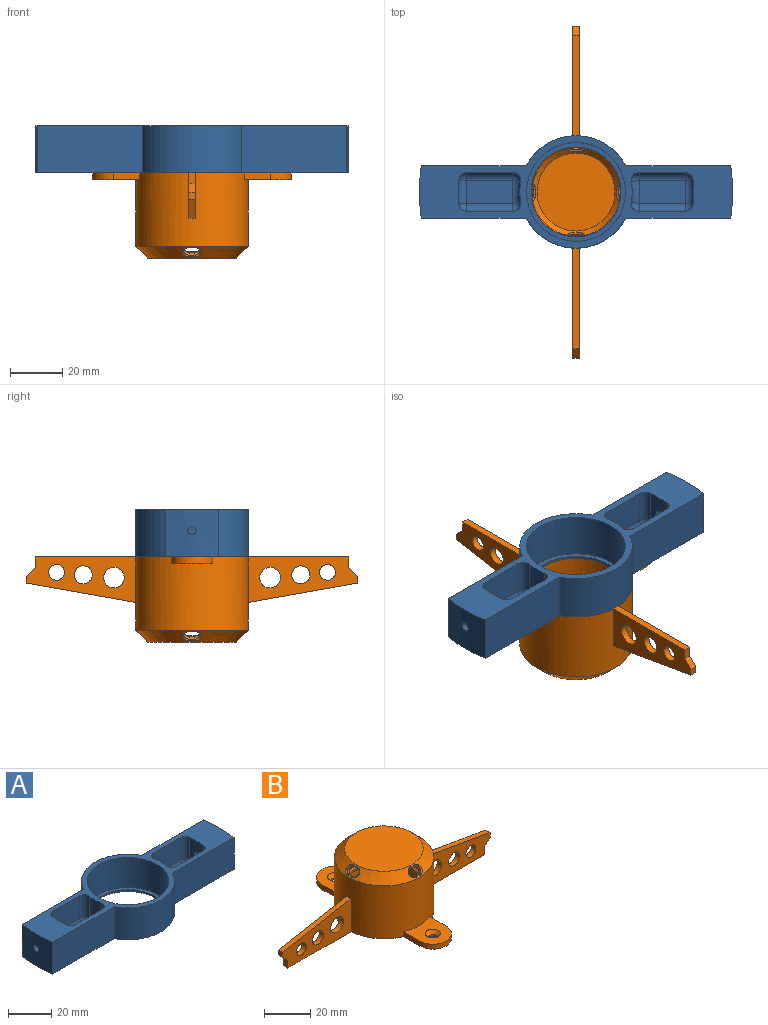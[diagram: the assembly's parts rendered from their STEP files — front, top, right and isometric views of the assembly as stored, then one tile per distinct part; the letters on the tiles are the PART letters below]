
ASSEMBLY  parts=2 mates=1
PART A: 49 faces, bbox 120x43x18 mm
  f0: cylinder r=60mm len=20mm, axis (0,0,-1), area 353.6mm2, adj f5,f10,f11,f12,f48
  f1: cylinder r=45mm len=12.6mm, axis (0,0,1), area 111mm2, adj f11,f36,f42,f43,f48
  f2: cylinder r=60mm len=20mm, axis (0,0,-1), area 353.6mm2, adj f7,f8,f11,f12,f47
  f3: cylinder r=45mm len=12.6mm, axis (0,0,1), area 111mm2, adj f11,f29,f30,f34,f47
  f4: cylinder r=17.2mm len=34.4mm, axis (0,0,-1), area 108.1mm2, adj f12,f21
  f5: plane 40.13x18mm, normal (0,-1,0), area 722.3mm2, adj f0,f6,f11,f12
  f6: cylinder r=21.5mm len=38.07mm, axis (0,0,-1), area 841.4mm2, adj f5,f7,f11,f12
  f7: plane 40.13x18mm, normal (0,-1,0), area 722.3mm2, adj f2,f6,f11,f12
  f8: plane 40.13x18mm, normal (0,1,0), area 722.3mm2, adj f2,f9,f11,f12
  f9: cylinder r=21.5mm len=38.07mm, axis (0,0,-1), area 841.4mm2, adj f8,f10,f11,f12
  f10: plane 40.13x18mm, normal (0,1,0), area 722.3mm2, adj f0,f9,f11,f12
  f11: plane 120x43mm, normal (0,0,1), area 1207.4mm2, adj f0,f1,f2,f3,f5,f6,f7,f8
  f12: plane 120x43mm, normal (0,0,-1), area 2083.7mm2, adj f0,f2,f4,f5,f6,f7,f8,f9
  f13: plane 17.9x8.8mm, normal (0,0,1), area 154.5mm2, adj f25,f28,f31,f34
  f14: plane 17.67x12.6mm, normal (0,1,0), area 222.6mm2, adj f11,f24,f30,f31
  f15: plane 17.67x12.6mm, normal (0,-1,0), area 222.6mm2, adj f11,f23,f28,f29
  f16: cylinder r=21.5mm len=12.6mm, axis (0,0,1), area 97.8mm2, adj f11,f23,f24,f25
  f17: plane 17.9x8.8mm, normal (0,0,1), area 154.5mm2, adj f37,f40,f43,f46
  f18: plane 17.67x12.6mm, normal (0,-1,0), area 222.6mm2, adj f11,f35,f36,f37
  f19: plane 17.67x12.6mm, normal (0,1,0), area 222.6mm2, adj f11,f41,f42,f46
  f20: cylinder r=21.5mm len=12.6mm, axis (0,0,1), area 97.8mm2, adj f11,f35,f40,f41
  f21: plane 37.8x37.8mm, normal (0,0,1), area 192.8mm2, adj f4,f22
  f22: cylinder r=18.9mm len=37.8mm, axis (0,0,1), area 2018.8mm2, adj f11,f21
  f23: cylinder r=3mm len=12.6mm, axis (0,0,1), area 66.2mm2, adj f11,f15,f16,f26
  f24: cylinder r=3mm len=12.6mm, axis (0,0,1), area 66.2mm2, adj f11,f14,f16,f27
  f25: torus R=24.5mm, axis (0,0,1), area 38.4mm2, adj f13,f16,f26,f27
  f26: sphere r=3mm, area 15.8mm2, adj f23,f25,f28
  f27: sphere r=3mm, area 15.8mm2, adj f24,f25,f31
  f28: cylinder r=3mm len=17.67mm, axis (1,0,0), area 83.3mm2, adj f13,f15,f26,f32
  f29: cylinder r=3mm len=12.6mm, axis (0,0,1), area 55.4mm2, adj f3,f11,f15,f32
  f30: cylinder r=3mm len=12.6mm, axis (0,0,1), area 55.4mm2, adj f3,f11,f14,f33
  f31: cylinder r=3mm len=17.67mm, axis (-1,0,0), area 83.3mm2, adj f13,f14,f27,f33
  f32: sphere r=3mm, area 13.2mm2, adj f28,f29,f34
  f33: sphere r=3mm, area 13.2mm2, adj f30,f31,f34
  f34: torus R=42mm, axis (0,0,1), area 43.4mm2, adj f3,f13,f32,f33
  f35: cylinder r=3mm len=12.6mm, axis (0,0,1), area 66.2mm2, adj f11,f18,f20,f38
  f36: cylinder r=3mm len=12.6mm, axis (0,0,1), area 55.4mm2, adj f1,f11,f18,f39
  f37: cylinder r=3mm len=17.67mm, axis (1,0,0), area 83.3mm2, adj f17,f18,f38,f39
  f38: sphere r=3mm, area 15.8mm2, adj f35,f37,f40
  f39: sphere r=3mm, area 13.2mm2, adj f36,f37,f43
  f40: torus R=24.5mm, axis (0,0,1), area 38.4mm2, adj f17,f20,f38,f44
  f41: cylinder r=3mm len=12.6mm, axis (0,0,1), area 66.2mm2, adj f11,f19,f20,f44
  f42: cylinder r=3mm len=12.6mm, axis (0,0,1), area 55.4mm2, adj f1,f11,f19,f45
  f43: torus R=42mm, axis (0,0,1), area 43.4mm2, adj f1,f17,f39,f45
  f44: sphere r=3mm, area 15.8mm2, adj f40,f41,f46
  f45: sphere r=3mm, area 13.2mm2, adj f42,f43,f46
  f46: cylinder r=3mm len=17.67mm, axis (-1,0,0), area 83.3mm2, adj f17,f19,f44,f45
  f47: cylinder r=1.6mm len=15.03mm, axis (-1,0,0), area 150.8mm2, adj f2,f3
  f48: cylinder r=1.6mm len=15.03mm, axis (1,0,0), area 150.8mm2, adj f0,f1
PART B: 89 faces, bbox 127x75.9x32.6 mm
  f0: cylinder r=21.5mm len=43mm, axis (0,0,-1), area 3617mm2, adj f2,f4,f5,f6,f8,f9,f11,f12
  f1: cylinder r=60mm len=4.01mm, axis (0,0,-1), area 10.4mm2, adj f5,f9,f12,f68
  f2: cone r=21.5mm half-angle=45deg, axis (0,0,-1), area 639.7mm2, adj f0,f13,f23,f24,f25,f26,f35,f36
  f3: cone r=18.9mm half-angle=45deg, axis (0,0,-1), area 644.6mm2, adj f17,f18,f27,f28,f29,f30,f39,f40
  f4: plane 42.04x7.42mm, normal (-0.17,0,0.98), area 110.9mm2, adj f0,f5,f9,f67
  f5: plane 42.03x17.41mm, normal (0,-1,0), area 440.6mm2, adj f0,f1,f4,f12,f67,f68,f83,f84
  f6: plane 42.03x17.41mm, normal (0,-1,0), area 440.6mm2, adj f0,f7,f11,f12,f69,f70,f86,f87
  f7: cylinder r=60mm len=4.01mm, axis (0,0,-1), area 10.4mm2, adj f6,f8,f12,f70
  f8: plane 42.03x17.41mm, normal (0,1,0), area 440.6mm2, adj f0,f7,f11,f12,f69,f70,f86,f87
  f9: plane 42.03x17.41mm, normal (0,1,0), area 440.6mm2, adj f0,f1,f4,f12,f67,f68,f83,f84
  f10: cylinder r=18.9mm len=37.8mm, axis (0,0,-1), area 1294.4mm2, adj f12,f14
  f11: plane 42.04x7.42mm, normal (0.17,0,0.98), area 110.9mm2, adj f0,f6,f8,f69
  f12: plane 120x75.91mm, normal (0,0,-1), area 1002mm2, adj f0,f1,f5,f6,f7,f8,f9,f10
  f13: plane 33.95x33.95mm, normal (0,0,1), area 905.5mm2, adj f2
  f14: cone r=18.9mm half-angle=45deg, axis (0,0,-1), area 318.1mm2, adj f10,f15
  f15: cylinder r=16.9mm len=33.8mm, axis (0,0,1), area 106.2mm2, adj f14,f16
  f16: cone r=16.9mm half-angle=45deg, axis (0,0,1), area 490.5mm2, adj f15,f17
  f17: cylinder r=19.9mm len=39.8mm, axis (0,0,1), area 1137.8mm2, adj f3,f16
  f18: plane 29.8x29.8mm, normal (0,0,-1), area 697.5mm2, adj f3
  f19: plane 2.2x1.15mm, normal (0,-0.71,-0.71), area 3.5mm2, adj f20,f22,f26,f30
  f20: cylinder r=2.1mm len=4.28mm, axis (0,0.71,-0.71), area 10.6mm2, adj f19,f21,f24,f28
  f21: plane 2.2x1.15mm, normal (0,0.71,0.71), area 3.5mm2, adj f20,f22,f23,f27
  f22: cylinder r=2.1mm len=4.28mm, axis (0,0.71,-0.71), area 10.6mm2, adj f19,f21,f25,f29
  f23: bspline ~11.26x1.06mm, area 1.7mm2, adj f2,f21,f24,f25
  f24: bspline ~3.69x3.68mm, area 5.9mm2, adj f2,f20,f23,f26
  f25: bspline ~3.69x3.68mm, area 5.9mm2, adj f2,f22,f23,f26
  f26: bspline ~11.33x1.14mm, area 1.8mm2, adj f2,f19,f24,f25
  f27: bspline ~11.08x1.08mm, area 1.7mm2, adj f3,f21,f28,f29
  f28: bspline ~3.69x3.68mm, area 5.3mm2, adj f3,f20,f27,f30
  f29: bspline ~3.69x3.68mm, area 5.3mm2, adj f3,f22,f27,f30
  f30: bspline ~11.12x1.15mm, area 1.7mm2, adj f3,f19,f28,f29
  f31: plane 2.2x1.15mm, normal (0.71,0,-0.71), area 3.5mm2, adj f32,f34,f38,f42
  f32: cylinder r=2.1mm len=4.28mm, axis (-0.71,0,-0.71), area 10.6mm2, adj f31,f33,f36,f40
  f33: plane 2.2x1.15mm, normal (-0.71,0,0.71), area 3.5mm2, adj f32,f34,f35,f39
  f34: cylinder r=2.1mm len=4.28mm, axis (-0.71,0,-0.71), area 10.6mm2, adj f31,f33,f37,f41
  f35: bspline ~11.26x1.06mm, area 1.7mm2, adj f2,f33,f36,f37
  f36: bspline ~3.69x3.68mm, area 5.9mm2, adj f2,f32,f35,f38
  f37: bspline ~3.69x3.68mm, area 5.9mm2, adj f2,f34,f35,f38
  f38: bspline ~11.33x1.14mm, area 1.8mm2, adj f2,f31,f36,f37
  f39: bspline ~11.08x1.08mm, area 1.7mm2, adj f3,f33,f40,f41
  f40: bspline ~3.69x3.68mm, area 5.3mm2, adj f3,f32,f39,f42
  f41: bspline ~3.69x3.68mm, area 5.3mm2, adj f3,f34,f39,f42
  f42: bspline ~7.79x1.15mm, area 1.7mm2, adj f3,f31,f40,f41
  f43: plane 2.2x1.15mm, normal (0,0.71,-0.71), area 3.5mm2, adj f44,f46,f50,f54
  f44: cylinder r=2.1mm len=4.28mm, axis (0,-0.71,-0.71), area 10.6mm2, adj f43,f45,f48,f52
  f45: plane 2.2x1.15mm, normal (0,-0.71,0.71), area 3.5mm2, adj f44,f46,f47,f51
  f46: cylinder r=2.1mm len=4.28mm, axis (0,-0.71,-0.71), area 10.6mm2, adj f43,f45,f49,f53
  f47: bspline ~11.26x1.06mm, area 1.7mm2, adj f2,f45,f48,f49
  f48: bspline ~3.69x3.68mm, area 5.9mm2, adj f2,f44,f47,f50
  f49: bspline ~3.69x3.68mm, area 5.9mm2, adj f2,f46,f47,f50
  f50: bspline ~11.33x1.14mm, area 1.8mm2, adj f2,f43,f48,f49
  f51: bspline ~11.08x1.08mm, area 1.7mm2, adj f3,f45,f52,f53
  f52: bspline ~3.69x3.68mm, area 5.3mm2, adj f3,f44,f51,f54
  f53: bspline ~3.69x3.68mm, area 5.3mm2, adj f3,f46,f51,f54
  f54: bspline ~7.79x1.15mm, area 1.7mm2, adj f3,f43,f52,f53
  f55: plane 2.2x1.15mm, normal (-0.71,0,-0.71), area 3.5mm2, adj f56,f58,f62,f66
  f56: cylinder r=2.1mm len=4.28mm, axis (0.71,0,-0.71), area 10.6mm2, adj f55,f57,f60,f64
  f57: plane 2.2x1.15mm, normal (0.71,0,0.71), area 3.5mm2, adj f56,f58,f59,f63
  f58: cylinder r=2.1mm len=4.28mm, axis (0.71,0,-0.71), area 10.6mm2, adj f55,f57,f61,f65
  f59: bspline ~11.26x1.06mm, area 1.7mm2, adj f2,f57,f60,f61
  f60: bspline ~3.69x3.68mm, area 5.9mm2, adj f2,f56,f59,f62
  f61: bspline ~3.69x3.68mm, area 5.9mm2, adj f2,f58,f59,f62
  f62: bspline ~11.33x1.14mm, area 1.8mm2, adj f2,f55,f60,f61
  f63: bspline ~11.08x1.08mm, area 1.7mm2, adj f3,f57,f64,f65
  f64: bspline ~3.69x3.68mm, area 5.3mm2, adj f3,f56,f63,f66
  f65: bspline ~3.69x3.68mm, area 5.3mm2, adj f3,f58,f63,f66
  f66: bspline ~11.12x1.15mm, area 1.7mm2, adj f3,f55,f64,f65
  f67: plane 2.6x2.5mm, normal (-1,0,0), area 6.5mm2, adj f4,f5,f9,f68
  f68: plane 3.5x3.5mm, normal (-0.71,0,-0.71), area 12.8mm2, adj f1,f5,f9,f67
  f69: plane 2.6x2.5mm, normal (1,0,0), area 6.5mm2, adj f6,f8,f11,f70
  f70: plane 3.5x3.5mm, normal (0.71,0,-0.71), area 12.8mm2, adj f6,f7,f8,f69
  f71: plane 10x2.6mm, normal (-1,0,0), area 26mm2, adj f0,f12,f73,f74
  f72: plane 10x2.6mm, normal (1,0,0), area 26mm2, adj f0,f12,f73,f74
  f73: cylinder r=8mm len=16mm, axis (0,0,-1), area 65.3mm2, adj f12,f71,f72,f74
  f74: plane 18x16mm, normal (0,0,1), area 210.8mm2, adj f0,f71,f72,f73,f76
  f75: cylinder r=1.6mm len=3.2mm, axis (0,0,1), area 9.6mm2, adj f12,f76
  f76: cone r=1.6mm half-angle=45deg, axis (0,0,1), area 35.6mm2, adj f74,f75
  f77: plane 10x2.6mm, normal (-1,0,0), area 26mm2, adj f0,f12,f78,f80
  f78: cylinder r=8mm len=16mm, axis (0,0,-1), area 65.3mm2, adj f12,f77,f79,f80
  f79: plane 10x2.6mm, normal (1,0,0), area 26mm2, adj f0,f12,f78,f80
  f80: plane 18x16mm, normal (0,0,1), area 210.8mm2, adj f0,f77,f78,f79,f82
  f81: cylinder r=1.6mm len=3.2mm, axis (0,0,1), area 9.6mm2, adj f12,f82
  f82: cone r=1.6mm half-angle=45deg, axis (0,0,1), area 35.6mm2, adj f80,f81
  f83: cylinder r=3.45mm len=6.91mm, axis (0,-1,0), area 56.4mm2, adj f5,f9
  f84: cylinder r=3.95mm len=7.91mm, axis (0,-1,0), area 64.6mm2, adj f5,f9
  f85: cylinder r=3.02mm len=6.04mm, axis (0,-1,0), area 49.3mm2, adj f5,f9
  f86: cylinder r=3.45mm len=6.91mm, axis (0,-1,0), area 56.4mm2, adj f6,f8
  f87: cylinder r=3.95mm len=7.91mm, axis (0,-1,0), area 64.6mm2, adj f6,f8
  f88: cylinder r=3.02mm len=6.04mm, axis (0,-1,0), area 49.3mm2, adj f6,f8
PLACE A t=(0,0,-6.1)mm
PLACE B rot(axis=(-0.71,-0.71,0),180deg) t=(0,0,-6.1)mm
MATE fastened A.f4 <-> B.f10  axis (0,0,1) through (0,0,-6.1)mm
